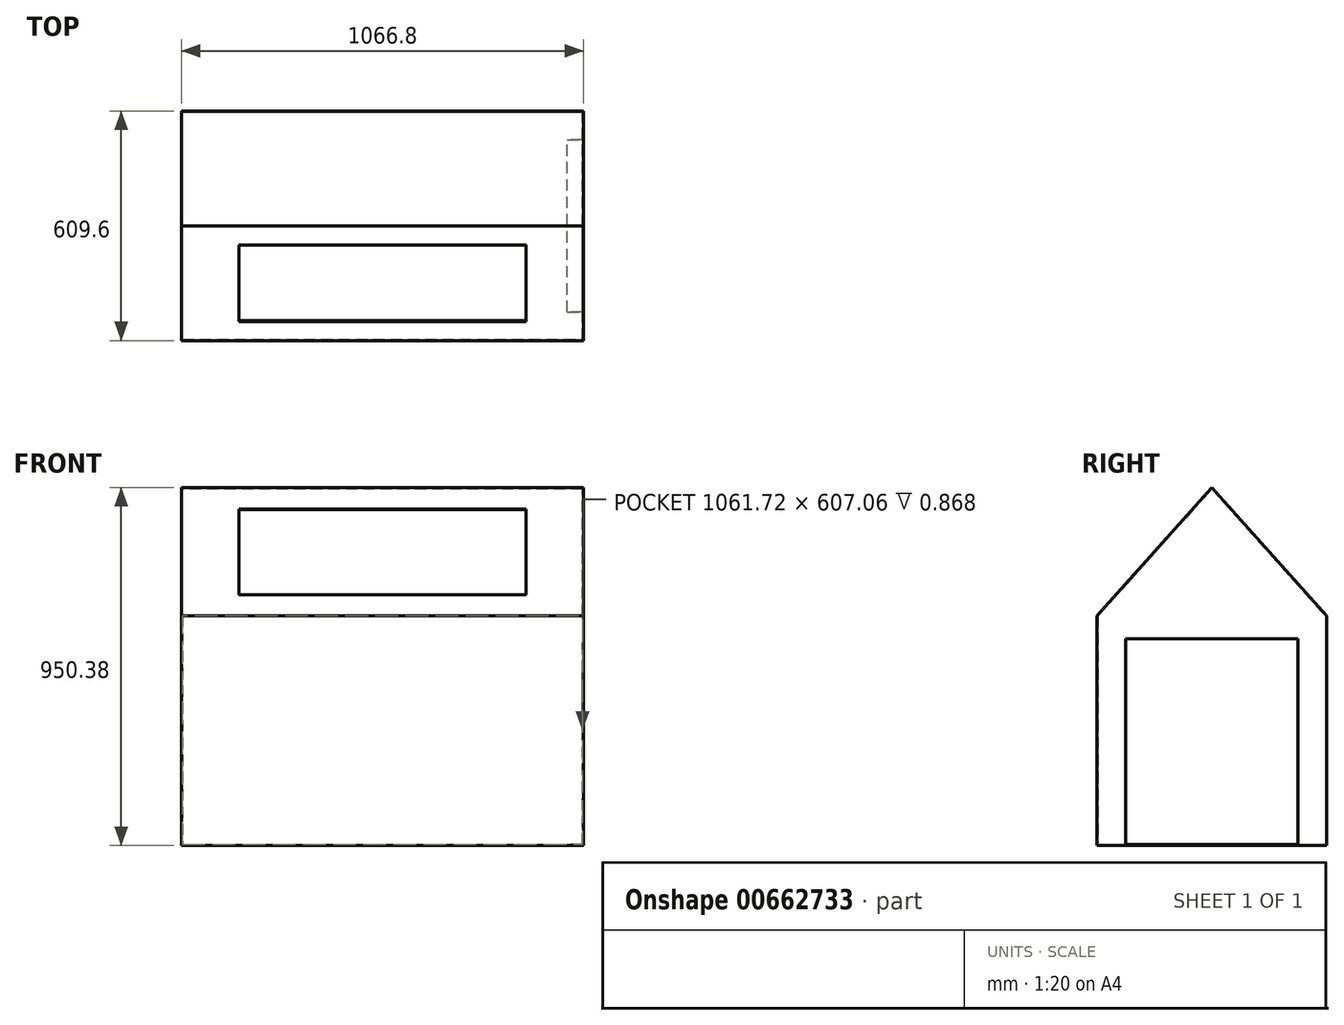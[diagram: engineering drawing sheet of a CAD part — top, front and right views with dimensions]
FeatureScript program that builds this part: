
annotation { "Feature Type Name" : "Feature", "Feature Type Description" : "" }
export const myFeature = defineFeature(function(context is Context, id is Id, definition is map)
    precondition{}
    {
        {
            var Q0;
            Q0=qCreatedBy(makeId("Front.planeOp"),FACE);
            var sketch = newSketch(context, id + "F0", { "sketchPlane" : qUnion([Q0])});
            skLineSegment(sketch, "E0.bottom", {"start": v(0, 0) * mm, "end": v(1066.8, 0) * mm});
            skLineSegment(sketch, "E0.top", {"start": v(0, -609.6) * mm, "end": v(1066.8, -609.6) * mm});
            skLineSegment(sketch, "E0.left", {"start": v(0, 0) * mm, "end": v(0, -609.6) * mm});
            skLineSegment(sketch, "E0.right", {"start": v(1066.8, 0) * mm, "end": v(1066.8, -609.6) * mm});
            skSolve(sketch);
        }
        {
            var Q0;
            Q0 = qSketchRegion(id + "F0", true);
            extrude(context, id + "F1", {"entities" : qUnion([Q0]), "depth" : 609.6 * mm, "offsetDistance" : 25.4 * mm});
        }
        {
            var Q0;
            Q0=makeQuery(id+"F1.opExtrude","SWEPT_FACE",FACE,{"disambiguationData":[OSD([sQuery(id+"F0.wireOp",EDGE,"E0.bottom")])]});
            shell(context, id + "F2", {"entities" : qUnion([Q0]), "thickness" : 2.54 * mm});
        }
        {
            var Q0;
            Q0=makeQuery(id+"F1.opExtrude","SWEPT_FACE",FACE,{"disambiguationData":[OSD([sQuery(id+"F0.wireOp",EDGE,"E0.right")])]});
            var sketch = newSketch(context, id + "F3", { "sketchPlane" : qUnion([Q0])});
            skLineSegment(sketch, "E1.bottom", {"start": v(-533.4, -609.6) * mm, "end": v(-76.2, -609.6) * mm});
            skLineSegment(sketch, "E1.top", {"start": v(-533.4, -60.96) * mm, "end": v(-76.2, -60.96) * mm});
            skLineSegment(sketch, "E1.left", {"start": v(-533.4, -609.6) * mm, "end": v(-533.4, -60.96) * mm});
            skLineSegment(sketch, "E1.right", {"start": v(-76.2, -609.6) * mm, "end": v(-76.2, -60.96) * mm});
            skSolve(sketch);
        }
        {
            var Q0;
            Q0=makeQuery(id+"F3.imprint","IMPRINT",FACE,{"disambiguationData":[TD([[makeQuery(id+"F3.imprint","IMPRINT",EDGE,{"derivedFrom":sQuery(id+"F3.wireOp",EDGE,"E1.bottom")}),1.0]])]});
            extrude(context, id + "F4", {"entities" : qUnion([Q0]), "operationType" : NewBodyOperationType.REMOVE, "oppositeDirection" : true, "depth" : 43.18 * mm, "offsetDistance" : 25.4 * mm});
        }
        {
            var Q0;
            Q0=makeQuery(id+"F1.opExtrude","SWEPT_FACE",FACE,{"disambiguationData":[OSD([sQuery(id+"F0.wireOp",EDGE,"E0.left")])]});
            var sketch = newSketch(context, id + "F5", { "sketchPlane" : qUnion([Q0])});
            skLineSegment(sketch, "E2", {"start": v(0, 0) * mm, "end": v(609.6, 0) * mm});
            skLineSegment(sketch, "E3", {"start": v(609.6, 0) * mm, "end": v(304.8, 340.78) * mm});
            skLineSegment(sketch, "E4", {"start": v(304.8, 340.78) * mm, "end": v(0, 0) * mm});
            skSolve(sketch);
        }
        {
            var Q0;
            Q0 = qSketchRegion(id + "F5", true);
            extrude(context, id + "F6", {"entities" : qUnion([Q0]), "operationType" : NewBodyOperationType.ADD, "oppositeDirection" : true, "depth" : 1066.8 * mm, "offsetDistance" : 25.4 * mm});
        }
        {
            var Q0;
            Q0=makeQuery(id+"F6.opExtrude","SWEPT_FACE",FACE,{"disambiguationData":[OSD([sQuery(id+"F5.wireOp",EDGE,"E2")])]});
            shell(context, id + "F7", {"entities" : qUnion([Q0]), "thickness" : 2.54 * mm});
        }
        {
            var Q0;
            Q0=makeQuery(id+"F6.opExtrude","SWEPT_FACE",FACE,{"disambiguationData":[OSD([sQuery(id+"F5.wireOp",EDGE,"E3")])]});
            var sketch = newSketch(context, id + "F8", { "sketchPlane" : qUnion([Q0])});
            skLineSegment(sketch, "E5.bottom", {"start": v(152.4, -25.4) * mm, "end": v(914.4, -25.4) * mm});
            skLineSegment(sketch, "E5.top", {"start": v(152.4, -330.2) * mm, "end": v(914.4, -330.2) * mm});
            skLineSegment(sketch, "E5.left", {"start": v(152.4, -25.4) * mm, "end": v(152.4, -330.2) * mm});
            skLineSegment(sketch, "E5.right", {"start": v(914.4, -25.4) * mm, "end": v(914.4, -330.2) * mm});
            skSolve(sketch);
        }
        {
            var Q0;
            Q0 = qSketchRegion(id + "F8", true);
            extrude(context, id + "F9", {"entities" : qUnion([Q0]), "operationType" : NewBodyOperationType.REMOVE, "oppositeDirection" : true, "depth" : 25.4 * mm, "offsetDistance" : 25.4 * mm});
        }
    });
